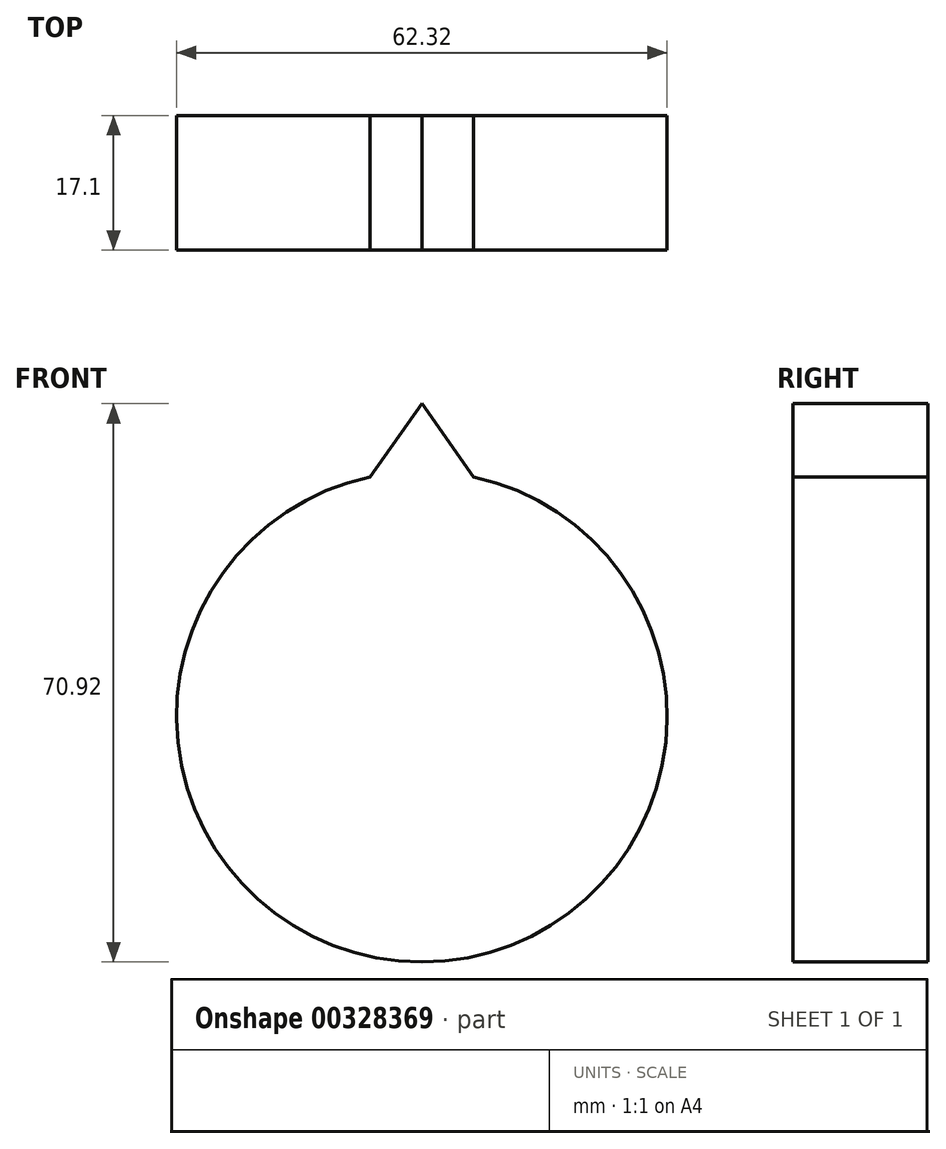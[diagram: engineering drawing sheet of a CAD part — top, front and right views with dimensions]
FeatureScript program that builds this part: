
annotation { "Feature Type Name" : "Feature", "Feature Type Description" : "" }
export const myFeature = defineFeature(function(context is Context, id is Id, definition is map)
    precondition{}
    {
        {
            var Q0;
            Q0=qCreatedBy(makeId("Front.planeOp"),FACE);
            var sketch = newSketch(context, id + "F0", { "sketchPlane" : qUnion([Q0])});
            skCircle(sketch, "E0", {"center": v(0, 0) * mm, "radius": 31.16 * mm});
            skSolve(sketch);
        }
        {
            var Q0;
            Q0 = qSketchRegion(id + "F0", true);
            extrude(context, id + "F1", {"entities" : qUnion([Q0]), "depth" : 17.1 * mm});
        }
        {
            var Q0;
            Q0=makeQuery(id+"F1.opExtrude","CAP_FACE",FACE,{"disambiguationData":[OSD([sQuery(id+"F0.wireOp",EDGE,"E0")])],"isStart":false});
            var sketch = newSketch(context, id + "F2", { "sketchPlane" : qUnion([Q0])});
            skLineSegment(sketch, "E1", {"start": v(-6.55, 30.46) * mm, "end": v(0, 39.76) * mm});
            skLineSegment(sketch, "E2", {"start": v(0, 39.76) * mm, "end": v(6.55, 30.46) * mm});
            skArc(sketch, "E3.0", {"start": v(6.55, 30.46) * mm, "mid": v(0, 31.16) * mm, "end": v(-6.55, 30.46) * mm});
            skSolve(sketch);
        }
        {
            var Q0;
            Q0=makeQuery(id+"F2.imprint","IMPRINT",FACE,{"disambiguationData":[TD([[makeQuery(id+"F2.imprint","IMPRINT",EDGE,{"derivedFrom":sQuery(id+"F2.wireOp",EDGE,"E1")}),-1.0]])]});
            var Q1;
            Q1=makeQuery(id+"F1.opExtrude","CAP_FACE",FACE,{"disambiguationData":[OSD([sQuery(id+"F0.wireOp",EDGE,"E0")])],"isStart":true});
            extrude(context, id + "F3", {"entities" : qUnion([Q0]), "operationType" : NewBodyOperationType.ADD, "endBound" : BoundingType.UP_TO_SURFACE, "oppositeDirection" : true, "endBoundEntityFace" : qUnion([Q1]), "depth" : 8 * mm});
        }
    });
